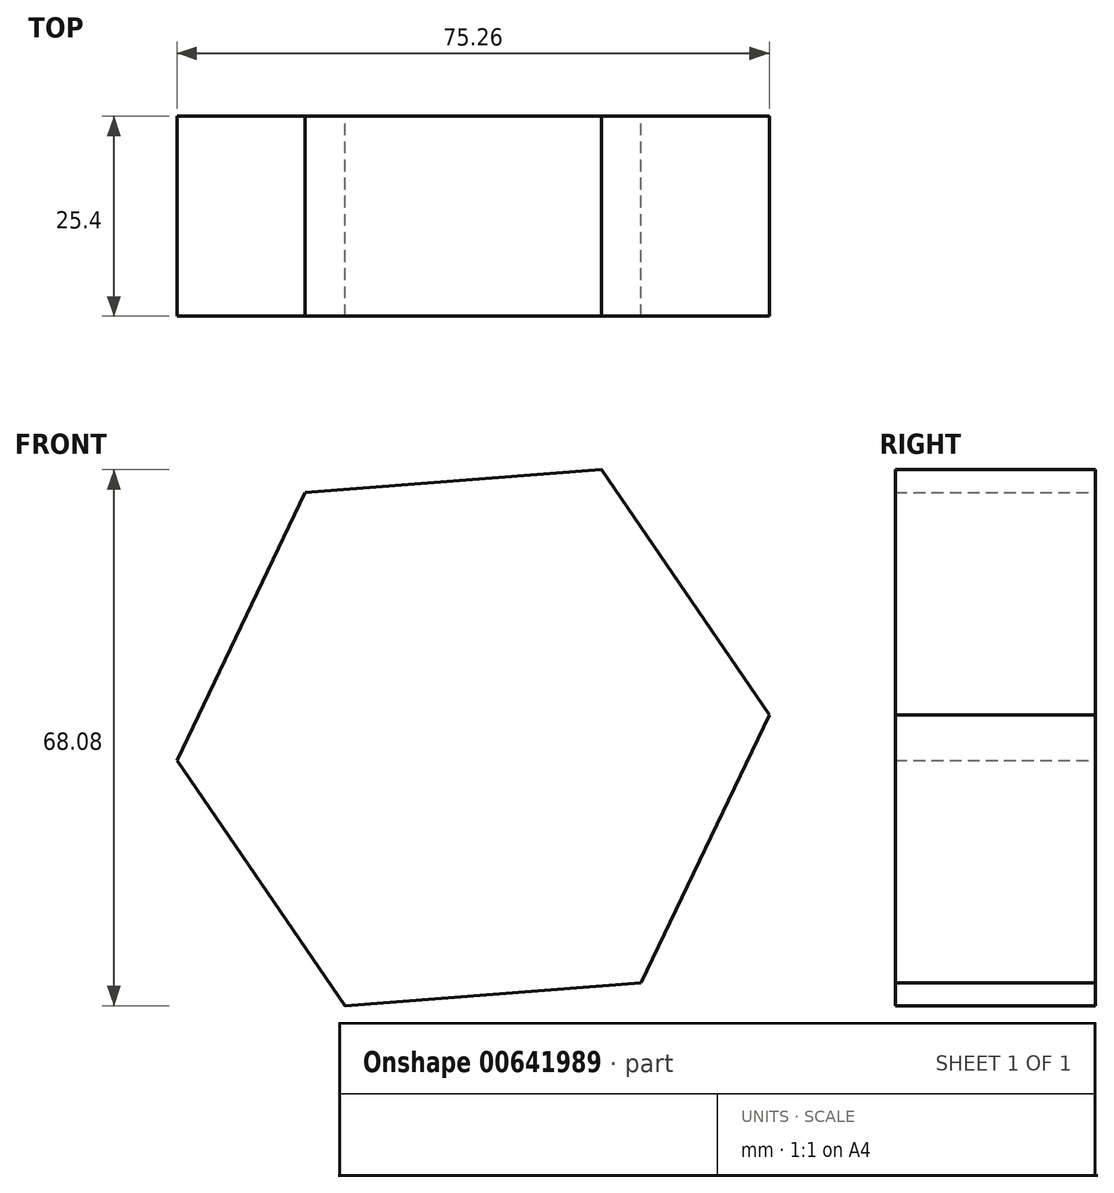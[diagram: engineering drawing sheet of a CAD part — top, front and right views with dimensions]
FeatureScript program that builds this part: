
annotation { "Feature Type Name" : "Feature", "Feature Type Description" : "" }
export const myFeature = defineFeature(function(context is Context, id is Id, definition is map)
    precondition{}
    {
        {
            var Q0;
            Q0=qCreatedBy(makeId("Front.planeOp"),FACE);
            var sketch = newSketch(context, id + "F0", { "sketchPlane" : qUnion([Q0])});
            skCircle(sketch, "E0.cCircle", {"center": v(0, 0) * mm, "radius": 32.68 * mm, "construction": true});
            skLineSegment(sketch, "E0.0", {"start": v(-37.63, -2.9) * mm, "end": v(-21.33, 31.13) * mm});
            skLineSegment(sketch, "E0.1", {"start": v(-21.33, 31.13) * mm, "end": v(16.3, 34.04) * mm});
            skLineSegment(sketch, "E0.2", {"start": v(16.3, 34.04) * mm, "end": v(37.63, 2.9) * mm});
            skLineSegment(sketch, "E0.3", {"start": v(37.63, 2.9) * mm, "end": v(21.33, -31.13) * mm});
            skLineSegment(sketch, "E0.4", {"start": v(21.33, -31.13) * mm, "end": v(-16.3, -34.04) * mm});
            skLineSegment(sketch, "E0.5", {"start": v(-16.3, -34.04) * mm, "end": v(-37.63, -2.9) * mm});
            skPoint(sketch, "E0.0.midPoint", {"position": v(-29.48, 14.11) * mm});
            skSolve(sketch);
        }
        {
            var Q0;
            Q0=makeQuery(id+"F0.imprint","IMPRINT",FACE,{"disambiguationData":[TD([[makeQuery(id+"F0.imprint","IMPRINT",EDGE,{"derivedFrom":sQuery(id+"F0.wireOp",EDGE,"E0.0")}),-1.0]])]});
            extrude(context, id + "F1", {"entities" : qUnion([Q0]), "depth" : 25.4 * mm, "offsetDistance" : 25.4 * mm});
        }
    });
